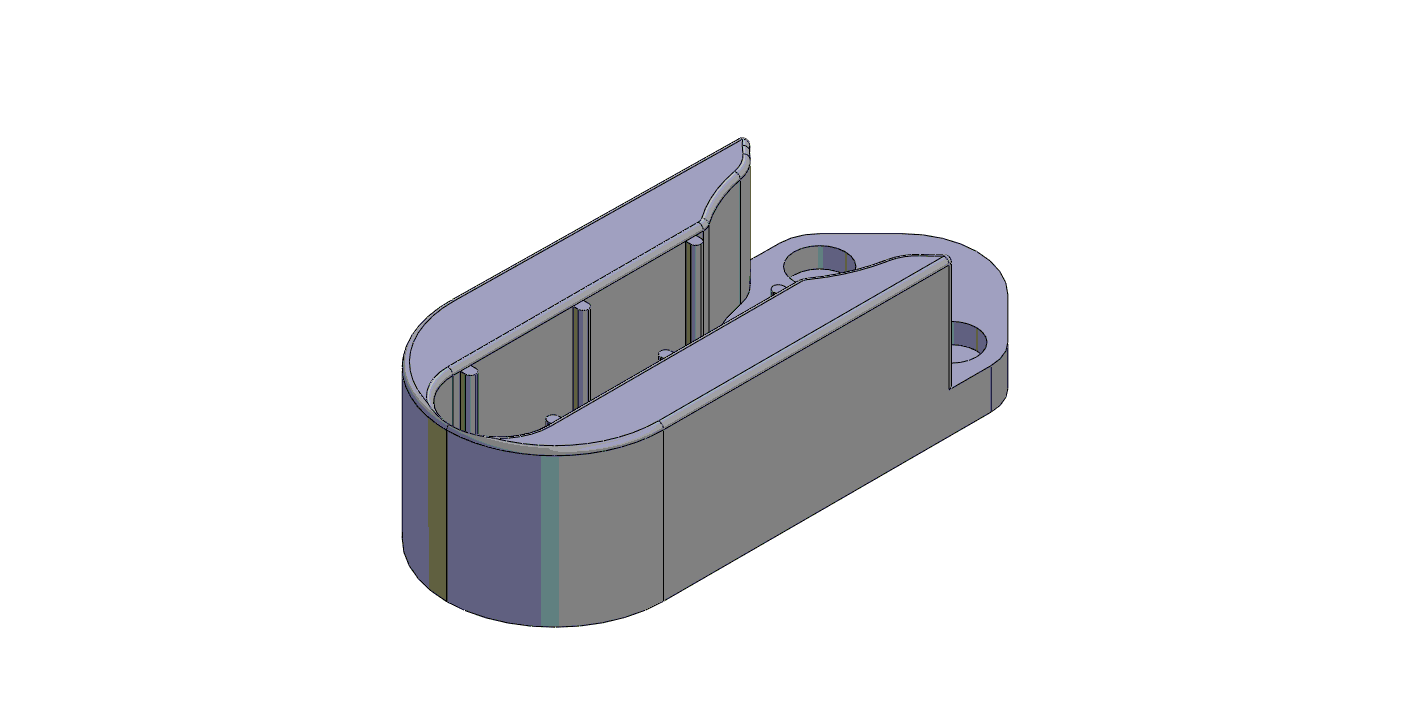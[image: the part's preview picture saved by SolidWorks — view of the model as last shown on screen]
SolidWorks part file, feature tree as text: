
SOLIDWORKS PART (.sldprt)
format: sldprt  version: not decoded by parser v0  size: 641,024 bytes
history: native  units: mm
features: sketch x11, extrude x6, cut_extrude x5, fillet x5, material x1 (+12 scaffold rows collapsed)
feature tree (40):
  scaffold x12  (default folders/planes/origin — collapsed)
  material  "Material <not specified>"
  sketch  "Sketch1"
  extrude  "Boss-Extrude1"  Depth=10mm
  sketch  "Sketch2"  dims[D1=0.0mm]
  extrude  "Boss-Extrude4"  Depth=101.6mm
  sketch  "Sketch4"  dims[D1=0.0mm]
  extrude  "Boss-Extrude5"  Depth=1mm
  sketch  "Sketch3"  dims[D1=0.0mm]
  cut_extrude  "Cut-Extrude3"  Depth=10mm
  fillet  "Fillet1"  Radius=27mm
  sketch  "Sketch5"  dims[D1=0.0mm]
  cut_extrude  "Cut-Extrude4"  Depth=63.5mm
  sketch  "Sketch6"  dims[D1=~5.175265mm]
  cut_extrude  "Cut-Extrude5"  Depth=5mm
  fillet  "Fillet3"  Radius=1.27mm
  fillet  "Fillet4"  Radius=1.27mm
  sketch  "Sketch7"
  extrude  "Boss-Extrude6"  [1 undecoded]
  sketch  "Sketch8"  dims[D1=12.7mm]
  cut_extrude  "Cut-Extrude6"  Depth=5mm
  sketch  "Sketch9"  dims[D1=2.54mm]
  extrude  "Boss-Extrude7"  Depth=2.54mm
  fillet  "Fillet5"  Radius=1.27mm
  sketch  "Sketch10"  dims[D1=2.54mm]
  extrude  "Boss-Extrude8"  Depth=2.54mm
  fillet  "Fillet6"  Radius=1.27mm
  sketch  "Sketch11"  dims[D1=12.7mm]
  cut_extrude  "Cut-Extrude8"  Depth=5mm
decode coverage: 24 of 27 modeling features carry decoded parameters
note: ~ marks probable driven/reference dimensions
note: 1 parameter value undecoded
note: suppression state not decoded; provenance and decode notes live in map.json
